# Revit family: Sink-Top_Mount-Kitchen-KOHLER-MARCATO-K-3676T
name_source: partatom
category: Plumbing Fixtures
revit_build: Autodesk Revit 2017 (Build: 20160225_1515(x64)
units: mm (PartAtom-declared; Revit-internal decimal feet)

## family parameters
Cut with Voids When Loaded = No
Host = Face
OmniClass Number = 23.31.13.00
OmniClass Title = Sinks
Part Type = Normal
Room Calculation Point = No
Round Connector Dimension = Use Diameter
Shared = No

## types (2) — shared parameters
ADA Compliant = No
Assembly Code = D2010400
CW Connection = No
Cold Water Inlet = Cold Water Inlet
Date Modified = 11/05/2020
Default Elevation = 36"
Description = Countertop Kitchen Basin
Drain Included = Yes
HW Connection = No
Height = 8 3/16"
Hot Water Inlet = Hot Water Inlet
Length = 18 1/2"
Manufacturer = KOHLER Co.
Master Format 2014 = 22 41 16
Master Format 2014 Name = Residential Lavatories and Sinks
Material = Stainless Steel
Product Documentation Link = https://files.kohler.com.cn
Product Name = MARCATO
Product Page URL = https://www.kohler.com.cn
URL = http://www.kohler.com.cn
Vent Connection = No
Waste Connection = Yes
Waste Water Outlet 1 = Waste Water Outlet 1
Waste Water Outlet 2 = Waste Water Outlet 2
WaterSense Certified = No
Width = 29 1/2"

## per-type parameters (varying)
| type | Finish | Model | Type |
| NA-Stainless | Kohler-Metal-NA-Stainless | K-3676T-2KD-NA | 1 |
| KS-Pearl Silver | Kohler-Metal-KS-Pearl_Silver | K-3676T-2KD-KA | 2 |

## geometry (parser evidence)
native form markers: Sweep x6
no freeform markers — native parametric forms only
